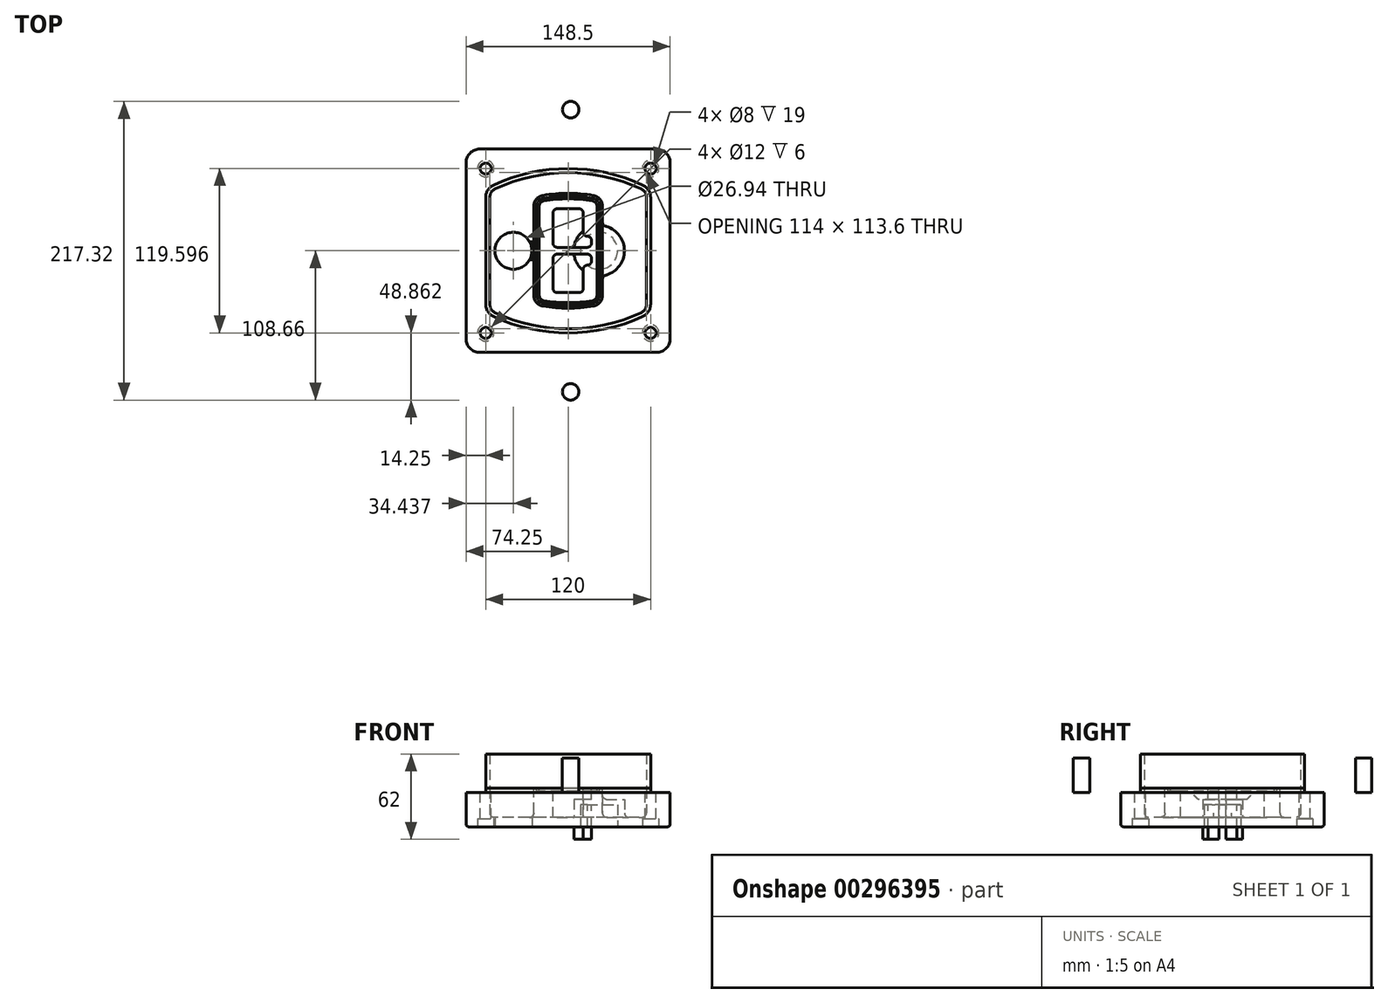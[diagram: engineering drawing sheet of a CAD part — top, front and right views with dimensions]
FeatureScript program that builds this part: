
annotation { "Feature Type Name" : "Feature", "Feature Type Description" : "" }
export const myFeature = defineFeature(function(context is Context, id is Id, definition is map)
    precondition{}
    {
        {
            var Q0;
            Q0=qCreatedBy(makeId("Top.planeOp"),FACE);
            var sketch = newSketch(context, id + "F0", { "sketchPlane" : qUnion([Q0])});
            skPoint(sketch, "E0.rect.middle", {"position": v(0, 0) * mm});
            skLineSegment(sketch, "E1.bottom", {"start": v(-64.25, -74) * mm, "end": v(64.25, -74) * mm});
            skLineSegment(sketch, "E1.top", {"start": v(-64.25, 74) * mm, "end": v(64.25, 74) * mm});
            skLineSegment(sketch, "E1.left", {"start": v(-74.25, -64) * mm, "end": v(-74.25, 64) * mm});
            skLineSegment(sketch, "E1.right", {"start": v(74.25, -64) * mm, "end": v(74.25, 64) * mm});
            skLineSegment(sketch, "E2", {"start": v(-74.25, 74) * mm, "end": v(74.25, -74) * mm, "construction": true});
            skLineSegment(sketch, "E3", {"start": v(74.25, 74) * mm, "end": v(-74.25, -74) * mm, "construction": true});
            skCircle(sketch, "E4", {"center": v(-60, 59.8) * mm, "radius": 4 * mm});
            skCircle(sketch, "E5", {"center": v(60, 59.8) * mm, "radius": 4 * mm});
            skCircle(sketch, "E6", {"center": v(60, -59.8) * mm, "radius": 4 * mm});
            skCircle(sketch, "E7", {"center": v(-60, -59.8) * mm, "radius": 4 * mm});
            skLineSegment(sketch, "E8", {"start": v(-60, 59.8) * mm, "end": v(60, 59.8) * mm, "construction": true});
            skLineSegment(sketch, "E9", {"start": v(60, 59.8) * mm, "end": v(60, -59.8) * mm, "construction": true});
            skLineSegment(sketch, "E10", {"start": v(60, -59.8) * mm, "end": v(-60, -59.8) * mm, "construction": true});
            skLineSegment(sketch, "E11", {"start": v(-60, -59.8) * mm, "end": v(-60, 59.8) * mm, "construction": true});
            skLineSegment(sketch, "E12", {"start": v(-60, 38.79) * mm, "end": v(-60, -38.79) * mm});
            skLineSegment(sketch, "E13", {"start": v(60, 38.79) * mm, "end": v(60, -38.79) * mm});
            skArc(sketch, "E14", {"start": v(54.2, 47.86) * mm, "mid": v(0, 59.8) * mm, "end": v(-54.2, 47.86) * mm});
            skArc(sketch, "E15", {"start": v(-54.2, -47.86) * mm, "mid": v(0, -59.8) * mm, "end": v(54.2, -47.86) * mm});
            skLineSegment(sketch, "E16", {"start": v(-60, 0) * mm, "end": v(60, 0) * mm, "construction": true});
            skPoint(sketch, "E17.visualSharp", {"position": v(-60, -45) * mm});
            skArc(sketch, "E17.filletArc", {"start": v(-60, -38.79) * mm, "mid": v(-58.43, -44.17) * mm, "end": v(-54.2, -47.86) * mm});
            skPoint(sketch, "E18.visualSharp", {"position": v(-60, 45) * mm});
            skArc(sketch, "E18.filletArc", {"start": v(-54.2, 47.86) * mm, "mid": v(-58.43, 44.17) * mm, "end": v(-60, 38.79) * mm});
            skPoint(sketch, "E19.visualSharp", {"position": v(60, 45) * mm});
            skArc(sketch, "E19.filletArc", {"start": v(60, 38.79) * mm, "mid": v(58.43, 44.17) * mm, "end": v(54.2, 47.86) * mm});
            skPoint(sketch, "E20.visualSharp", {"position": v(60, -45) * mm});
            skArc(sketch, "E20.filletArc", {"start": v(54.2, -47.86) * mm, "mid": v(58.43, -44.17) * mm, "end": v(60, -38.79) * mm});
            skPoint(sketch, "E21.visualSharp", {"position": v(-74.25, 74) * mm});
            skArc(sketch, "E21.filletArc", {"start": v(-64.25, 74) * mm, "mid": v(-71.32, 71.07) * mm, "end": v(-74.25, 64) * mm});
            skPoint(sketch, "E22.visualSharp", {"position": v(74.25, 74) * mm});
            skArc(sketch, "E22.filletArc", {"start": v(74.25, 64) * mm, "mid": v(71.32, 71.07) * mm, "end": v(64.25, 74) * mm});
            skPoint(sketch, "E23.visualSharp", {"position": v(74.25, -74) * mm});
            skArc(sketch, "E23.filletArc", {"start": v(64.25, -74) * mm, "mid": v(71.32, -71.07) * mm, "end": v(74.25, -64) * mm});
            skPoint(sketch, "E24.visualSharp", {"position": v(-74.25, -74) * mm});
            skArc(sketch, "E24.filletArc", {"start": v(-74.25, -64) * mm, "mid": v(-71.32, -71.07) * mm, "end": v(-64.25, -74) * mm});
            skArc(sketch, "E25.0", {"start": v(57, 38.79) * mm, "mid": v(55.9, 42.56) * mm, "end": v(52.94, 45.14) * mm});
            skLineSegment(sketch, "E25.1", {"start": v(57, 38.79) * mm, "end": v(57, -38.79) * mm});
            skArc(sketch, "E25.2", {"start": v(52.94, -45.14) * mm, "mid": v(55.9, -42.56) * mm, "end": v(57, -38.79) * mm});
            skArc(sketch, "E25.3", {"start": v(-52.94, -45.14) * mm, "mid": v(0, -56.8) * mm, "end": v(52.94, -45.14) * mm});
            skArc(sketch, "E25.4", {"start": v(-57, -38.79) * mm, "mid": v(-55.9, -42.56) * mm, "end": v(-52.94, -45.14) * mm});
            skArc(sketch, "E25.5", {"start": v(52.94, 45.14) * mm, "mid": v(0, 56.8) * mm, "end": v(-52.94, 45.14) * mm});
            skLineSegment(sketch, "E25.6", {"start": v(-57, 38.79) * mm, "end": v(-57, -38.79) * mm});
            skArc(sketch, "E25.7", {"start": v(-52.94, 45.14) * mm, "mid": v(-55.9, 42.56) * mm, "end": v(-57, 38.79) * mm});
            skArc(sketch, "E26.0", {"start": v(-55.88, 51.5) * mm, "mid": v(-61.8, 46.33) * mm, "end": v(-64, 38.79) * mm});
            skArc(sketch, "E26.1", {"start": v(55.88, 51.5) * mm, "mid": v(0, 63.8) * mm, "end": v(-55.88, 51.5) * mm});
            skArc(sketch, "E26.2", {"start": v(64, 38.79) * mm, "mid": v(61.8, 46.33) * mm, "end": v(55.88, 51.5) * mm});
            skLineSegment(sketch, "E26.3", {"start": v(64, 38.79) * mm, "end": v(64, -38.79) * mm});
            skArc(sketch, "E26.4", {"start": v(55.88, -51.5) * mm, "mid": v(61.8, -46.33) * mm, "end": v(64, -38.79) * mm});
            skLineSegment(sketch, "E26.5", {"start": v(-64, 38.79) * mm, "end": v(-64, -38.79) * mm});
            skArc(sketch, "E26.6", {"start": v(-55.88, -51.5) * mm, "mid": v(0, -63.8) * mm, "end": v(55.88, -51.5) * mm});
            skArc(sketch, "E26.7", {"start": v(-64, -38.79) * mm, "mid": v(-61.8, -46.33) * mm, "end": v(-55.88, -51.5) * mm});
            skSolve(sketch);
        }
        {
            var Q0;
            Q0=makeQuery(id+"F0.imprint","IMPRINT",FACE,{"disambiguationData":[TD([[makeQuery(id+"F0.imprint","IMPRINT",EDGE,{"derivedFrom":sQuery(id+"F0.wireOp",EDGE,"E1.bottom")}),1.0]])]});
            var Q1;
            Q1=makeQuery(id+"F0.imprint","IMPRINT",FACE,{"disambiguationData":[TD([[makeQuery(id+"F0.imprint","IMPRINT",EDGE,{"derivedFrom":sQuery(id+"F0.wireOp",EDGE,"E12")}),1.0]])]});
            var Q2;
            Q2=makeQuery(id+"F0.imprint","IMPRINT",FACE,{"disambiguationData":[TD([[makeQuery(id+"F0.imprint","IMPRINT",EDGE,{"derivedFrom":sQuery(id+"F0.wireOp",EDGE,"E25.0")}),1.0]])]});
            var Q3;
            Q3=makeQuery(id+"F0.imprint","IMPRINT",FACE,{"disambiguationData":[TD([[makeQuery(id+"F0.imprint","IMPRINT",EDGE,{"derivedFrom":sQuery(id+"F0.wireOp",EDGE,"E12")}),-1.0]])]});
            extrude(context, id + "F1", {"entities" : qUnion([Q0, Q1, Q2, Q3]), "oppositeDirection" : true, "depth" : 25 * mm});
        }
        {
            var Q0;
            Q0=makeQuery(id+"F0.imprint","IMPRINT",FACE,{"disambiguationData":[TD([[makeQuery(id+"F0.imprint","IMPRINT",EDGE,{"derivedFrom":sQuery(id+"F0.wireOp",EDGE,"E12")}),1.0]])]});
            extrude(context, id + "F2", {"entities" : qUnion([Q0]), "operationType" : NewBodyOperationType.ADD, "depth" : 3 * mm});
        }
        {
            var Q0;
            Q0=makeQuery(id+"F0.imprint","IMPRINT",FACE,{"disambiguationData":[TD([[makeQuery(id+"F0.imprint","IMPRINT",EDGE,{"derivedFrom":sQuery(id+"F0.wireOp",EDGE,"E25.0")}),1.0]])]});
            extrude(context, id + "F3", {"entities" : qUnion([Q0]), "operationType" : NewBodyOperationType.REMOVE, "oppositeDirection" : true, "depth" : 18 * mm});
        }
        {
            var Q0;
            Q0=makeQuery(id+"F2.opExtrude","CAP_FACE",FACE,{"disambiguationData":[OSD([sQuery(id+"F0.wireOp",EDGE,"E12"),sQuery(id+"F0.wireOp",EDGE,"E13"),sQuery(id+"F0.wireOp",EDGE,"E14"),sQuery(id+"F0.wireOp",EDGE,"E15"),sQuery(id+"F0.wireOp",EDGE,"E17.filletArc"),sQuery(id+"F0.wireOp",EDGE,"E18.filletArc"),sQuery(id+"F0.wireOp",EDGE,"E19.filletArc"),sQuery(id+"F0.wireOp",EDGE,"E20.filletArc"),sQuery(id+"F0.wireOp",EDGE,"E25.0"),sQuery(id+"F0.wireOp",EDGE,"E25.1"),sQuery(id+"F0.wireOp",EDGE,"E25.2"),sQuery(id+"F0.wireOp",EDGE,"E25.3"),sQuery(id+"F0.wireOp",EDGE,"E25.4"),sQuery(id+"F0.wireOp",EDGE,"E25.5"),sQuery(id+"F0.wireOp",EDGE,"E25.6"),sQuery(id+"F0.wireOp",EDGE,"E25.7")])],"isStart":false});
            var sketch = newSketch(context, id + "F4", { "sketchPlane" : qUnion([Q0])});
            skArc(sketch, "E27.0", {"start": v(-18.32, -40.28) * mm, "mid": v(0, -41.8) * mm, "end": v(18.32, -40.28) * mm});
            skArc(sketch, "E28.0", {"start": v(18.32, 40.28) * mm, "mid": v(0, 41.8) * mm, "end": v(-18.32, 40.28) * mm});
            skLineSegment(sketch, "E29", {"start": v(-25, 32.39) * mm, "end": v(-25, -32.39) * mm});
            skLineSegment(sketch, "E30", {"start": v(25, 32.39) * mm, "end": v(25, -32.39) * mm});
            skLineSegment(sketch, "E31", {"start": v(-25, 38.95) * mm, "end": v(25, 38.95) * mm, "construction": true});
            skLineSegment(sketch, "E32", {"start": v(-25, -38.95) * mm, "end": v(25, -38.95) * mm, "construction": true});
            skPoint(sketch, "E33.visualSharp", {"position": v(-25, 38.95) * mm});
            skArc(sketch, "E33.filletArc", {"start": v(-18.32, 40.28) * mm, "mid": v(-23.1, 37.56) * mm, "end": v(-25, 32.39) * mm});
            skPoint(sketch, "E34.visualSharp", {"position": v(25, 38.95) * mm});
            skArc(sketch, "E34.filletArc", {"start": v(25, 32.39) * mm, "mid": v(23.1, 37.56) * mm, "end": v(18.32, 40.28) * mm});
            skPoint(sketch, "E35.visualSharp", {"position": v(25, -38.95) * mm});
            skArc(sketch, "E35.filletArc", {"start": v(18.32, -40.28) * mm, "mid": v(23.1, -37.56) * mm, "end": v(25, -32.39) * mm});
            skPoint(sketch, "E36.visualSharp", {"position": v(-25, -38.95) * mm});
            skArc(sketch, "E36.filletArc", {"start": v(-25, -32.39) * mm, "mid": v(-23.1, -37.56) * mm, "end": v(-18.32, -40.28) * mm});
            skArc(sketch, "E37.0", {"start": v(52.94, 45.14) * mm, "mid": v(0, 56.8) * mm, "end": v(-52.94, 45.14) * mm});
            skArc(sketch, "E37.1", {"start": v(-52.94, 45.14) * mm, "mid": v(-55.9, 42.56) * mm, "end": v(-57, 38.79) * mm});
            skLineSegment(sketch, "E37.2", {"start": v(-57, 38.79) * mm, "end": v(-57, -38.79) * mm});
            skArc(sketch, "E37.3", {"start": v(-57, -38.79) * mm, "mid": v(-55.9, -42.56) * mm, "end": v(-52.94, -45.14) * mm});
            skArc(sketch, "E37.4", {"start": v(-52.94, -45.14) * mm, "mid": v(0, -56.8) * mm, "end": v(52.94, -45.14) * mm});
            skArc(sketch, "E37.5", {"start": v(52.94, -45.14) * mm, "mid": v(55.9, -42.56) * mm, "end": v(57, -38.79) * mm});
            skLineSegment(sketch, "E37.6", {"start": v(57, 38.79) * mm, "end": v(57, -38.79) * mm});
            skArc(sketch, "E37.7", {"start": v(57, 38.79) * mm, "mid": v(55.9, 42.56) * mm, "end": v(52.94, 45.14) * mm});
            skLineSegment(sketch, "E38.0", {"start": v(23, 32.39) * mm, "end": v(23, -32.39) * mm});
            skArc(sketch, "E38.1", {"start": v(17.99, -38.3) * mm, "mid": v(21.58, -36.26) * mm, "end": v(23, -32.39) * mm});
            skArc(sketch, "E38.2", {"start": v(-17.99, -38.3) * mm, "mid": v(0, -39.8) * mm, "end": v(17.99, -38.3) * mm});
            skArc(sketch, "E38.3", {"start": v(-23, -32.39) * mm, "mid": v(-21.58, -36.26) * mm, "end": v(-17.99, -38.3) * mm});
            skLineSegment(sketch, "E38.4", {"start": v(-23, 32.39) * mm, "end": v(-23, -32.39) * mm});
            skArc(sketch, "E38.5", {"start": v(23, 32.39) * mm, "mid": v(21.58, 36.26) * mm, "end": v(17.99, 38.3) * mm});
            skArc(sketch, "E38.6", {"start": v(-17.99, 38.3) * mm, "mid": v(-21.58, 36.26) * mm, "end": v(-23, 32.39) * mm});
            skArc(sketch, "E38.7", {"start": v(17.99, 38.3) * mm, "mid": v(0, 39.8) * mm, "end": v(-17.99, 38.3) * mm});
            skArc(sketch, "E39.0", {"start": v(21, 32.39) * mm, "mid": v(20.05, 34.97) * mm, "end": v(17.66, 36.33) * mm});
            skLineSegment(sketch, "E39.1", {"start": v(21, 32.39) * mm, "end": v(21, -32.39) * mm});
            skArc(sketch, "E39.2", {"start": v(17.66, -36.33) * mm, "mid": v(20.05, -34.97) * mm, "end": v(21, -32.39) * mm});
            skArc(sketch, "E39.3", {"start": v(-17.66, -36.33) * mm, "mid": v(0, -37.8) * mm, "end": v(17.66, -36.33) * mm});
            skArc(sketch, "E39.4", {"start": v(-21, -32.39) * mm, "mid": v(-20.05, -34.97) * mm, "end": v(-17.66, -36.33) * mm});
            skArc(sketch, "E39.5", {"start": v(17.66, 36.33) * mm, "mid": v(0, 37.8) * mm, "end": v(-17.66, 36.33) * mm});
            skLineSegment(sketch, "E39.6", {"start": v(-21, 32.39) * mm, "end": v(-21, -32.39) * mm});
            skArc(sketch, "E39.7", {"start": v(-17.66, 36.33) * mm, "mid": v(-20.05, 34.97) * mm, "end": v(-21, 32.39) * mm});
            skLineSegment(sketch, "E40", {"start": v(-25, 0) * mm, "end": v(25, 0) * mm, "construction": true});
            skLineSegment(sketch, "E41", {"start": v(-11, 5.5) * mm, "end": v(-11, 27.5) * mm});
            skLineSegment(sketch, "E42", {"start": v(-8, 30.5) * mm, "end": v(8, 30.5) * mm});
            skLineSegment(sketch, "E43", {"start": v(11, 27.5) * mm, "end": v(11, 13.5) * mm});
            skLineSegment(sketch, "E44", {"start": v(14, 10.5) * mm, "end": v(14, 10.5) * mm});
            skLineSegment(sketch, "E45", {"start": v(17, 7.5) * mm, "end": v(17, 5.5) * mm});
            skLineSegment(sketch, "E46", {"start": v(14, 2.5) * mm, "end": v(-8, 2.5) * mm});
            skPoint(sketch, "E47.visualSharp", {"position": v(-11, 30.5) * mm});
            skArc(sketch, "E47.filletArc", {"start": v(-8, 30.5) * mm, "mid": v(-10.12, 29.62) * mm, "end": v(-11, 27.5) * mm});
            skPoint(sketch, "E48.visualSharp", {"position": v(11, 30.5) * mm});
            skArc(sketch, "E48.filletArc", {"start": v(11, 27.5) * mm, "mid": v(10.12, 29.62) * mm, "end": v(8, 30.5) * mm});
            skPoint(sketch, "E49.visualSharp", {"position": v(11, 10.5) * mm});
            skArc(sketch, "E49.filletArc", {"start": v(11, 13.5) * mm, "mid": v(11.88, 11.38) * mm, "end": v(14, 10.5) * mm});
            skPoint(sketch, "E50.visualSharp", {"position": v(17, 10.5) * mm});
            skArc(sketch, "E50.filletArc", {"start": v(17, 7.5) * mm, "mid": v(16.12, 9.62) * mm, "end": v(14, 10.5) * mm});
            skPoint(sketch, "E51.visualSharp", {"position": v(17, 2.5) * mm});
            skArc(sketch, "E51.filletArc", {"start": v(14, 2.5) * mm, "mid": v(16.12, 3.38) * mm, "end": v(17, 5.5) * mm});
            skPoint(sketch, "E52.visualSharp", {"position": v(-11, 2.5) * mm});
            skArc(sketch, "E52.filletArc", {"start": v(-11, 5.5) * mm, "mid": v(-10.12, 3.38) * mm, "end": v(-8, 2.5) * mm});
            skLineSegment(sketch, "E53.0.MirrorCS", {"start": v(14, -2.5) * mm, "end": v(-8, -2.5) * mm});
            skArc(sketch, "E54.0.MirrorCS", {"start": v(-11, -5.5) * mm, "mid": v(-10.12, -3.38) * mm, "end": v(-8, -2.5) * mm});
            skLineSegment(sketch, "E55.0.MirrorCS", {"start": v(-11, -5.5) * mm, "end": v(-11, -27.5) * mm});
            skArc(sketch, "E56.0.MirrorCS", {"start": v(-8, -30.5) * mm, "mid": v(-10.12, -29.62) * mm, "end": v(-11, -27.5) * mm});
            skLineSegment(sketch, "E57.0.MirrorCS", {"start": v(-8, -30.5) * mm, "end": v(8, -30.5) * mm});
            skArc(sketch, "E58.0.MirrorCS", {"start": v(11, -27.5) * mm, "mid": v(10.12, -29.62) * mm, "end": v(8, -30.5) * mm});
            skLineSegment(sketch, "E59.0.MirrorCS", {"start": v(11, -27.5) * mm, "end": v(11, -13.5) * mm});
            skArc(sketch, "E60.0.MirrorCS", {"start": v(11, -13.5) * mm, "mid": v(11.88, -11.38) * mm, "end": v(14, -10.5) * mm});
            skArc(sketch, "E61.0.MirrorCS", {"start": v(17, -7.5) * mm, "mid": v(16.12, -9.62) * mm, "end": v(14, -10.5) * mm});
            skLineSegment(sketch, "E62.0.MirrorCS", {"start": v(17, -7.5) * mm, "end": v(17, -5.5) * mm});
            skArc(sketch, "E63.0.MirrorCS", {"start": v(14, -2.5) * mm, "mid": v(16.12, -3.38) * mm, "end": v(17, -5.5) * mm});
            skSolve(sketch);
        }
        {
            var Q0;
            Q0=makeQuery(id+"F4.imprint","IMPRINT",FACE,{"disambiguationData":[TD([[makeQuery(id+"F4.imprint","IMPRINT",EDGE,{"derivedFrom":sQuery(id+"F4.wireOp",EDGE,"E27.0")}),1.0]])]});
            var Q1;
            Q1=makeQuery(id+"F4.imprint","IMPRINT",FACE,{"disambiguationData":[TD([[makeQuery(id+"F4.imprint","IMPRINT",EDGE,{"derivedFrom":sQuery(id+"F4.wireOp",EDGE,"E38.0")}),-1.0]])]});
            var Q2;
            Q2=makeQuery(id+"F4.imprint","IMPRINT",FACE,{"disambiguationData":[TD([[makeQuery(id+"F4.imprint","IMPRINT",EDGE,{"derivedFrom":sQuery(id+"F4.wireOp",EDGE,"E39.0")}),1.0]])]});
            extrude(context, id + "F5", {"entities" : qUnion([Q0, Q1, Q2]), "operationType" : NewBodyOperationType.ADD, "endBound" : BoundingType.UP_TO_NEXT, "oppositeDirection" : true, "depth" : 25 * mm});
        }
        {
            var Q0;
            Q0=makeQuery(id+"F4.imprint","IMPRINT",FACE,{"disambiguationData":[TD([[makeQuery(id+"F4.imprint","IMPRINT",EDGE,{"derivedFrom":sQuery(id+"F4.wireOp",EDGE,"E38.0")}),-1.0]])]});
            extrude(context, id + "F6", {"entities" : qUnion([Q0]), "operationType" : NewBodyOperationType.REMOVE, "oppositeDirection" : true, "depth" : 2 * mm});
        }
        {
            var Q0;
            Q0=makeQuery(id+"F1.opExtrude","CAP_FACE",FACE,{"disambiguationData":[OSD([sQuery(id+"F0.wireOp",EDGE,"E1.bottom"),sQuery(id+"F0.wireOp",EDGE,"E1.top"),sQuery(id+"F0.wireOp",EDGE,"E1.left"),sQuery(id+"F0.wireOp",EDGE,"E1.right"),sQuery(id+"F0.wireOp",EDGE,"E4"),sQuery(id+"F0.wireOp",EDGE,"E5"),sQuery(id+"F0.wireOp",EDGE,"E6"),sQuery(id+"F0.wireOp",EDGE,"E7"),sQuery(id+"F0.wireOp",EDGE,"E21.filletArc"),sQuery(id+"F0.wireOp",EDGE,"E22.filletArc"),sQuery(id+"F0.wireOp",EDGE,"E23.filletArc"),sQuery(id+"F0.wireOp",EDGE,"E24.filletArc")])],"isStart":false});
            var sketch = newSketch(context, id + "F7", { "sketchPlane" : qUnion([Q0])});
            skCircle(sketch, "E64", {"center": v(22.5, 0) * mm, "radius": 13.47 * mm});
            skCircle(sketch, "E65", {"center": v(-39.81, 0) * mm, "radius": 13.47 * mm});
            skLineSegment(sketch, "E66", {"start": v(74.25, 0) * mm, "end": v(-74.25, 0) * mm});
            skCircle(sketch, "E67", {"center": v(22.5, 0) * mm, "radius": 18.47 * mm});
            skCircle(sketch, "E68", {"center": v(60, -59.8) * mm, "radius": 6 * mm});
            skCircle(sketch, "E69", {"center": v(-60, -59.8) * mm, "radius": 6 * mm});
            skCircle(sketch, "E70", {"center": v(-60, 59.8) * mm, "radius": 6 * mm});
            skCircle(sketch, "E71", {"center": v(60, 59.8) * mm, "radius": 6 * mm});
            skSolve(sketch);
        }
        {
            var Q0;
            {var subQ1=sQuery(id+"F7.wireOp",EDGE,"E66");var subQ4=sQuery(id+"F7.wireOp",EDGE,"E64");var subQ6=makeQuery(id+"F7.imprint","INTERSECT",VERTEX,{"disambiguationData":[OD(0.0)],"derivedFrom":[subQ4,subQ1]});Q0=makeQuery(id+"F7.imprint","IMPRINT",FACE,{"disambiguationData":[TD([[makeQuery(id+"F7.imprint","IMPRINT",EDGE,{"disambiguationData":[TD([[subQ6,-1.0]])],"derivedFrom":subQ4}),-1.0]])]});}
            var Q1;
            {var subQ0=sQuery(id+"F7.wireOp",EDGE,"E66");var subQ1=sQuery(id+"F7.wireOp",EDGE,"E64");var subQ3=makeQuery(id+"F7.imprint","INTERSECT",VERTEX,{"disambiguationData":[OD(0.0)],"derivedFrom":[subQ1,subQ0]});Q1=makeQuery(id+"F7.imprint","IMPRINT",FACE,{"disambiguationData":[TD([[makeQuery(id+"F7.imprint","IMPRINT",EDGE,{"disambiguationData":[TD([[subQ3,-1.0]])],"derivedFrom":subQ1}),1.0]])]});}
            var Q2;
            {var subQ0=sQuery(id+"F7.wireOp",EDGE,"E66");var subQ1=sQuery(id+"F7.wireOp",EDGE,"E64");var subQ3=makeQuery(id+"F7.imprint","INTERSECT",VERTEX,{"disambiguationData":[OD(0.0)],"derivedFrom":[subQ1,subQ0]});Q2=makeQuery(id+"F7.imprint","IMPRINT",FACE,{"disambiguationData":[TD([[makeQuery(id+"F7.imprint","IMPRINT",EDGE,{"disambiguationData":[TD([[subQ3,1.0]])],"derivedFrom":subQ1}),1.0]])]});}
            var Q3;
            {var subQ1=sQuery(id+"F7.wireOp",EDGE,"E66");var subQ4=sQuery(id+"F7.wireOp",EDGE,"E64");var subQ6=makeQuery(id+"F7.imprint","INTERSECT",VERTEX,{"disambiguationData":[OD(0.0)],"derivedFrom":[subQ4,subQ1]});Q3=makeQuery(id+"F7.imprint","IMPRINT",FACE,{"disambiguationData":[TD([[makeQuery(id+"F7.imprint","IMPRINT",EDGE,{"disambiguationData":[TD([[subQ6,1.0]])],"derivedFrom":subQ4}),-1.0]])]});}
            extrude(context, id + "F8", {"entities" : qUnion([Q0, Q1, Q2, Q3]), "operationType" : NewBodyOperationType.ADD, "oppositeDirection" : true, "depth" : 20 * mm});
        }
        {
            var Q0;
            {var subQ0=sQuery(id+"F7.wireOp",EDGE,"E66");var subQ1=sQuery(id+"F7.wireOp",EDGE,"E64");var subQ3=makeQuery(id+"F7.imprint","INTERSECT",VERTEX,{"disambiguationData":[OD(0.0)],"derivedFrom":[subQ1,subQ0]});Q0=makeQuery(id+"F7.imprint","IMPRINT",FACE,{"disambiguationData":[TD([[makeQuery(id+"F7.imprint","IMPRINT",EDGE,{"disambiguationData":[TD([[subQ3,-1.0]])],"derivedFrom":subQ1}),1.0]])]});}
            var Q1;
            {var subQ0=sQuery(id+"F7.wireOp",EDGE,"E66");var subQ1=sQuery(id+"F7.wireOp",EDGE,"E64");var subQ3=makeQuery(id+"F7.imprint","INTERSECT",VERTEX,{"disambiguationData":[OD(0.0)],"derivedFrom":[subQ1,subQ0]});Q1=makeQuery(id+"F7.imprint","IMPRINT",FACE,{"disambiguationData":[TD([[makeQuery(id+"F7.imprint","IMPRINT",EDGE,{"disambiguationData":[TD([[subQ3,1.0]])],"derivedFrom":subQ1}),1.0]])]});}
            extrude(context, id + "F9", {"entities" : qUnion([Q0, Q1]), "operationType" : NewBodyOperationType.REMOVE, "oppositeDirection" : true, "depth" : 16 * mm});
        }
        {
            var Q0;
            {var subQ0=sQuery(id+"F7.wireOp",EDGE,"E66");var subQ1=sQuery(id+"F7.wireOp",EDGE,"E65");var subQ3=makeQuery(id+"F7.imprint","INTERSECT",VERTEX,{"disambiguationData":[OD(0.0)],"derivedFrom":[subQ1,subQ0]});Q0=makeQuery(id+"F7.imprint","IMPRINT",FACE,{"disambiguationData":[TD([[makeQuery(id+"F7.imprint","IMPRINT",EDGE,{"disambiguationData":[TD([[subQ3,-1.0]])],"derivedFrom":subQ1}),1.0]])]});}
            var Q1;
            {var subQ0=sQuery(id+"F7.wireOp",EDGE,"E66");var subQ1=sQuery(id+"F7.wireOp",EDGE,"E65");var subQ3=makeQuery(id+"F7.imprint","INTERSECT",VERTEX,{"disambiguationData":[OD(0.0)],"derivedFrom":[subQ1,subQ0]});Q1=makeQuery(id+"F7.imprint","IMPRINT",FACE,{"disambiguationData":[TD([[makeQuery(id+"F7.imprint","IMPRINT",EDGE,{"disambiguationData":[TD([[subQ3,1.0]])],"derivedFrom":subQ1}),1.0]])]});}
            extrude(context, id + "F10", {"entities" : qUnion([Q0, Q1]), "operationType" : NewBodyOperationType.REMOVE, "oppositeDirection" : true, "depth" : 25 * mm});
        }
        {
            var Q0;
            Q0=makeQuery(id+"F7.imprint","IMPRINT",FACE,{"disambiguationData":[TD([[makeQuery(id+"F7.imprint","IMPRINT",EDGE,{"derivedFrom":sQuery(id+"F7.wireOp",EDGE,"E68")}),1.0]])]});
            var Q1;
            Q1=makeQuery(id+"F7.imprint","IMPRINT",FACE,{"disambiguationData":[TD([[makeQuery(id+"F7.imprint","IMPRINT",EDGE,{"derivedFrom":makeQuery(id+"F1.opExtrude","CAP_EDGE",EDGE,{"disambiguationData":[OSD([sQuery(id+"F0.wireOp",EDGE,"E5")])],"isStart":false})}),-1.0]])]});
            var Q2;
            Q2=makeQuery(id+"F7.imprint","IMPRINT",FACE,{"disambiguationData":[TD([[makeQuery(id+"F7.imprint","IMPRINT",EDGE,{"derivedFrom":sQuery(id+"F7.wireOp",EDGE,"E69")}),1.0]])]});
            var Q3;
            Q3=makeQuery(id+"F7.imprint","IMPRINT",FACE,{"disambiguationData":[TD([[makeQuery(id+"F7.imprint","IMPRINT",EDGE,{"derivedFrom":makeQuery(id+"F1.opExtrude","CAP_EDGE",EDGE,{"disambiguationData":[OSD([sQuery(id+"F0.wireOp",EDGE,"E4")])],"isStart":false})}),-1.0]])]});
            var Q4;
            Q4=makeQuery(id+"F7.imprint","IMPRINT",FACE,{"disambiguationData":[TD([[makeQuery(id+"F7.imprint","IMPRINT",EDGE,{"derivedFrom":sQuery(id+"F7.wireOp",EDGE,"E70")}),1.0]])]});
            var Q5;
            Q5=makeQuery(id+"F7.imprint","IMPRINT",FACE,{"disambiguationData":[TD([[makeQuery(id+"F7.imprint","IMPRINT",EDGE,{"derivedFrom":makeQuery(id+"F1.opExtrude","CAP_EDGE",EDGE,{"disambiguationData":[OSD([sQuery(id+"F0.wireOp",EDGE,"E7")])],"isStart":false})}),-1.0]])]});
            var Q6;
            Q6=makeQuery(id+"F7.imprint","IMPRINT",FACE,{"disambiguationData":[TD([[makeQuery(id+"F7.imprint","IMPRINT",EDGE,{"derivedFrom":sQuery(id+"F7.wireOp",EDGE,"E71")}),1.0]])]});
            var Q7;
            Q7=makeQuery(id+"F7.imprint","IMPRINT",FACE,{"disambiguationData":[TD([[makeQuery(id+"F7.imprint","IMPRINT",EDGE,{"derivedFrom":makeQuery(id+"F1.opExtrude","CAP_EDGE",EDGE,{"disambiguationData":[OSD([sQuery(id+"F0.wireOp",EDGE,"E6")])],"isStart":false})}),-1.0]])]});
            extrude(context, id + "F11", {"entities" : qUnion([Q0, Q1, Q2, Q3, Q4, Q5, Q6, Q7]), "operationType" : NewBodyOperationType.REMOVE, "oppositeDirection" : true, "depth" : 6 * mm});
        }
        {
            var Q0;
            Q0=makeQuery(id+"F9.boolean.opBoolean","COPY",FACE,{"derivedFrom":makeQuery(id+"F9.opExtrude","CAP_FACE",FACE,{"disambiguationData":[OSD([sQuery(id+"F7.wireOp",EDGE,"E64")])],"isStart":false})});
            var sketch = newSketch(context, id + "F12", { "sketchPlane" : qUnion([Q0])});
            skArc(sketch, "E72.0", {"start": v(11, 14.45) * mm, "mid": v(6.45, 9.13) * mm, "end": v(4.2, 2.5) * mm});
            skArc(sketch, "E72.1", {"start": v(4.2, -2.5) * mm, "mid": v(6.45, -9.13) * mm, "end": v(11, -14.45) * mm});
            skLineSegment(sketch, "E73", {"start": v(4.2, -2.5) * mm, "end": v(14, -2.5) * mm});
            skLineSegment(sketch, "E74.0", {"start": v(14, 2.5) * mm, "end": v(4.2, 2.5) * mm});
            skArc(sketch, "E74.1", {"start": v(14, 2.5) * mm, "mid": v(16.12, 3.38) * mm, "end": v(17, 5.5) * mm});
            skLineSegment(sketch, "E74.2", {"start": v(17, 7.5) * mm, "end": v(17, 5.5) * mm});
            skArc(sketch, "E74.3", {"start": v(17, 7.5) * mm, "mid": v(16.12, 9.62) * mm, "end": v(14, 10.5) * mm});
            skArc(sketch, "E74.4", {"start": v(11, 13.5) * mm, "mid": v(11.88, 11.38) * mm, "end": v(14, 10.5) * mm});
            skLineSegment(sketch, "E74.5", {"start": v(11, 14.45) * mm, "end": v(11, 13.5) * mm});
            skLineSegment(sketch, "E74.7", {"start": v(14, -2.5) * mm, "end": v(4.2, -2.5) * mm});
            skArc(sketch, "E74.8", {"start": v(14, -2.5) * mm, "mid": v(16.12, -3.38) * mm, "end": v(17, -5.5) * mm});
            skLineSegment(sketch, "E74.9", {"start": v(17, -7.5) * mm, "end": v(17, -5.5) * mm});
            skArc(sketch, "E74.10", {"start": v(17, -7.5) * mm, "mid": v(16.12, -9.62) * mm, "end": v(14, -10.5) * mm});
            skArc(sketch, "E74.11", {"start": v(11, -13.5) * mm, "mid": v(11.88, -11.38) * mm, "end": v(14, -10.5) * mm});
            skLineSegment(sketch, "E74.12", {"start": v(11, -14.45) * mm, "end": v(11, -13.5) * mm});
            skPoint(sketch, "E75.orphan", {"position": v(11, -27.5) * mm});
            skPoint(sketch, "E76.orphan", {"position": v(-8, -2.5) * mm});
            skPoint(sketch, "E77.orphan", {"position": v(-8, 2.5) * mm});
            skPoint(sketch, "E78.orphan", {"position": v(11, 27.5) * mm});
            skSolve(sketch);
        }
        {
            var Q0;
            {var subQ7=sQuery(id+"F12.wireOp",EDGE,"E72.0");var subQ14=sQuery(id+"F12.wireOp",EDGE,"E72.1");var subQ16=sQuery(id+"F12.wireOp",EDGE,"E74.1");var subQ18=sQuery(id+"F12.wireOp",EDGE,"E74.8");Q0=qUnion([makeQuery(id+"F12.imprint","IMPRINT",FACE,{"disambiguationData":[TD([[makeQuery(id+"F12.imprint","IMPRINT",EDGE,{"derivedFrom":subQ7}),1.0]])]}),makeQuery(id+"F12.imprint","IMPRINT",FACE,{"disambiguationData":[TD([[makeQuery(id+"F12.imprint","IMPRINT",EDGE,{"derivedFrom":subQ14}),1.0]])]}),makeQuery(id+"F12.imprint","IMPRINT",FACE,{"disambiguationData":[TD([[makeQuery(id+"F12.imprint","IMPRINT",EDGE,{"derivedFrom":subQ16}),1.0]])]}),makeQuery(id+"F12.imprint","IMPRINT",FACE,{"disambiguationData":[TD([[makeQuery(id+"F12.imprint","IMPRINT",EDGE,{"derivedFrom":subQ18}),-1.0]])]})]);}
            var Q1;
            Q1=makeQuery(id+"F5.boolean.opBoolean","SPLIT",FACE,{"disambiguationData":[TD([makeQuery(id+"F5.opExtrude","SWEPT_FACE",FACE,{"disambiguationData":[OSD([sQuery(id+"F4.wireOp",EDGE,"E41")])]})])],"derivedFrom":makeQuery(id+"F3.boolean.opBoolean","COPY",FACE,{"derivedFrom":makeQuery(id+"F3.opExtrude","CAP_FACE",FACE,{"disambiguationData":[OSD([sQuery(id+"F0.wireOp",EDGE,"E25.0"),sQuery(id+"F0.wireOp",EDGE,"E25.1"),sQuery(id+"F0.wireOp",EDGE,"E25.2"),sQuery(id+"F0.wireOp",EDGE,"E25.3"),sQuery(id+"F0.wireOp",EDGE,"E25.4"),sQuery(id+"F0.wireOp",EDGE,"E25.5"),sQuery(id+"F0.wireOp",EDGE,"E25.6"),sQuery(id+"F0.wireOp",EDGE,"E25.7")])],"isStart":false})})});
            extrude(context, id + "F13", {"entities" : qUnion([Q0]), "operationType" : NewBodyOperationType.REMOVE, "endBound" : BoundingType.UP_TO_SURFACE, "endBoundEntityFace" : qUnion([Q1]), "depth" : 25 * mm});
        }
        {
            var Q0;
            Q0=makeQuery(id+"F3.boolean.opBoolean","COPY",EDGE,{"derivedFrom":makeQuery(id+"F3.opExtrude","CAP_EDGE",EDGE,{"disambiguationData":[OSD([sQuery(id+"F0.wireOp",EDGE,"E25.6")])],"isStart":false})});
            var Q1;
            Q1=makeQuery(id+"F8.boolean.opBoolean","INTERSECT",EDGE,{"derivedFrom":[makeQuery(id+"F5.opExtrude","SWEPT_FACE",FACE,{"disambiguationData":[OSD([sQuery(id+"F4.wireOp",EDGE,"E30")])]}),makeQuery(id+"F8.opExtrude","CAP_FACE",FACE,{"disambiguationData":[OSD([sQuery(id+"F7.wireOp",EDGE,"E67")])],"isStart":false})]});
            var Q2;
            Q2=makeQuery(id+"F8.boolean.opBoolean","INTERSECT",EDGE,{"disambiguationData":[OD(1.0)],"derivedFrom":[makeQuery(id+"F5.opExtrude","SWEPT_FACE",FACE,{"disambiguationData":[OSD([sQuery(id+"F4.wireOp",EDGE,"E30")])]}),makeQuery(id+"F8.opExtrude","SWEPT_FACE",FACE,{"disambiguationData":[OSD([sQuery(id+"F7.wireOp",EDGE,"E67")])]})]});
            var Q3;
            {var subQ0=sQuery(id+"F4.wireOp",EDGE,"E30");Q3=makeQuery(id+"F8.boolean.opBoolean","SPLIT",EDGE,{"disambiguationData":[TD([makeQuery(id+"F5.opExtrude","SWEPT_FACE",FACE,{"disambiguationData":[OSD([sQuery(id+"F4.wireOp",EDGE,"E35.filletArc")])]})])],"derivedFrom":makeQuery(id+"F5.opExtrude","CAP_EDGE",EDGE,{"disambiguationData":[OSD([subQ0])],"isStart":false})});}
            var Q4;
            {var subQ0=sQuery(id+"F0.wireOp",EDGE,"E25.7");var subQ1=sQuery(id+"F0.wireOp",EDGE,"E25.1");var subQ2=sQuery(id+"F0.wireOp",EDGE,"E25.6");var subQ3=sQuery(id+"F0.wireOp",EDGE,"E25.5");var subQ4=sQuery(id+"F0.wireOp",EDGE,"E25.4");var subQ5=sQuery(id+"F0.wireOp",EDGE,"E25.0");var subQ6=sQuery(id+"F0.wireOp",EDGE,"E25.2");var subQ7=sQuery(id+"F0.wireOp",EDGE,"E25.3");Q4=makeQuery(id+"F8.boolean.opBoolean","INTERSECT",EDGE,{"derivedFrom":[makeQuery(id+"F5.boolean.opBoolean","SPLIT",FACE,{"disambiguationData":[TD([makeQuery(id+"F2.opExtrude","SWEPT_FACE",FACE,{"disambiguationData":[OSD([subQ5])]})])],"derivedFrom":makeQuery(id+"F3.boolean.opBoolean","COPY",FACE,{"derivedFrom":makeQuery(id+"F3.opExtrude","CAP_FACE",FACE,{"disambiguationData":[OSD([subQ5,subQ1,subQ6,subQ7,subQ4,subQ3,subQ2,subQ0])],"isStart":false})})}),makeQuery(id+"F8.opExtrude","SWEPT_FACE",FACE,{"disambiguationData":[OSD([sQuery(id+"F7.wireOp",EDGE,"E67")])]})]});}
            var Q5;
            Q5=makeQuery(id+"F8.boolean.opBoolean","INTERSECT",EDGE,{"disambiguationData":[OD(0.0)],"derivedFrom":[makeQuery(id+"F5.opExtrude","SWEPT_FACE",FACE,{"disambiguationData":[OSD([sQuery(id+"F4.wireOp",EDGE,"E30")])]}),makeQuery(id+"F8.opExtrude","SWEPT_FACE",FACE,{"disambiguationData":[OSD([sQuery(id+"F7.wireOp",EDGE,"E67")])]})]});
            fillet(context, id + "F14", {"entities" : qUnion([Q0, Q1, Q2, Q3, Q4, Q5]), "radius" : 3 * mm, "tangentPropagation" : true, "allowEdgeOverflow" : false});
        }
        {
            var Q0;
            Q0=makeQuery(id+"F1.opExtrude","CAP_EDGE",EDGE,{"disambiguationData":[OSD([sQuery(id+"F0.wireOp",EDGE,"E1.bottom")])],"isStart":false});
            fillet(context, id + "F15", {"entities" : qUnion([Q0]), "radius" : 2 * mm, "tangentPropagation" : true, "allowEdgeOverflow" : false});
        }
        {
            var Q0;
            Q0 = qSketchRegion(id + "F12", true);
            extrude(context, id + "F16", {"entities" : qUnion([Q0]), "operationType" : NewBodyOperationType.ADD, "depth" : 25 * mm});
        }
        {
            var Q0;
            Q0=qCreatedBy(makeId("Top.planeOp"),FACE);
            var sketch = newSketch(context, id + "F17", { "sketchPlane" : qUnion([Q0])});
            skLineSegment(sketch, "E79", {"start": v(26.76, 75.63) * mm, "end": v(16.86, 90.66) * mm});
            skLineSegment(sketch, "E80", {"start": v(16.86, 90.66) * mm, "end": v(16.86, 102.66) * mm});
            skArc(sketch, "E81", {"start": v(16.86, 102.66) * mm, "mid": v(1.86, 117.66) * mm, "end": v(-13.14, 102.66) * mm});
            skLineSegment(sketch, "E82", {"start": v(-13.14, 102.66) * mm, "end": v(-13.14, 90.66) * mm});
            skLineSegment(sketch, "E83", {"start": v(-13.14, 90.66) * mm, "end": v(-21.62, 74.78) * mm});
            skCircle(sketch, "E84", {"center": v(1.86, 102.66) * mm, "radius": 6 * mm});
            skLineSegment(sketch, "E85", {"start": v(1.86, 102.66) * mm, "end": v(1.86, 72.66) * mm, "construction": true});
            skLineSegment(sketch, "E86", {"start": v(-74.8, 0) * mm, "end": v(74.55, 0) * mm, "construction": true});
            skLineSegment(sketch, "E87.MirrorCS", {"start": v(-13.14, -238.66) * mm, "end": v(-21.62, -222.78) * mm});
            skLineSegment(sketch, "E88.MirrorCS", {"start": v(-13.14, -250.66) * mm, "end": v(-13.14, -238.66) * mm});
            skArc(sketch, "E89.MirrorCS", {"start": v(16.86, -250.66) * mm, "mid": v(1.86, -265.66) * mm, "end": v(-13.14, -250.66) * mm});
            skLineSegment(sketch, "E90.MirrorCS", {"start": v(16.86, -238.66) * mm, "end": v(16.86, -250.66) * mm});
            skLineSegment(sketch, "E91.MirrorCS", {"start": v(26.76, -223.63) * mm, "end": v(16.86, -238.66) * mm});
            skLineSegment(sketch, "E92.MirrorCS", {"start": v(1.86, -250.66) * mm, "end": v(1.86, -220.66) * mm, "construction": true});
            skLineSegment(sketch, "E93.MirrorCS", {"start": v(-13.14, -90.66) * mm, "end": v(-21.62, -74.78) * mm});
            skLineSegment(sketch, "E94.MirrorCS", {"start": v(1.86, -102.66) * mm, "end": v(1.86, -72.66) * mm, "construction": true});
            skCircle(sketch, "E95.MirrorC", {"center": v(1.86, -102.66) * mm, "radius": 6 * mm});
            skArc(sketch, "E96.MirrorCS", {"start": v(16.86, -102.66) * mm, "mid": v(1.86, -117.66) * mm, "end": v(-13.14, -102.66) * mm});
            skLineSegment(sketch, "E97.MirrorCS", {"start": v(16.86, -90.66) * mm, "end": v(16.86, -102.66) * mm});
            skLineSegment(sketch, "E98.MirrorCS", {"start": v(-13.14, -102.66) * mm, "end": v(-13.14, -90.66) * mm});
            skLineSegment(sketch, "E99.MirrorCS", {"start": v(26.76, -75.63) * mm, "end": v(16.86, -90.66) * mm});
            skSolve(sketch);
        }
        {
            var Q0;
            Q0=makeQuery(id+"F2.opExtrude","CAP_FACE",FACE,{"disambiguationData":[OSD([sQuery(id+"F0.wireOp",EDGE,"E12"),sQuery(id+"F0.wireOp",EDGE,"E13"),sQuery(id+"F0.wireOp",EDGE,"E14"),sQuery(id+"F0.wireOp",EDGE,"E15"),sQuery(id+"F0.wireOp",EDGE,"E17.filletArc"),sQuery(id+"F0.wireOp",EDGE,"E18.filletArc"),sQuery(id+"F0.wireOp",EDGE,"E19.filletArc"),sQuery(id+"F0.wireOp",EDGE,"E20.filletArc"),sQuery(id+"F0.wireOp",EDGE,"E25.0"),sQuery(id+"F0.wireOp",EDGE,"E25.1"),sQuery(id+"F0.wireOp",EDGE,"E25.2"),sQuery(id+"F0.wireOp",EDGE,"E25.3"),sQuery(id+"F0.wireOp",EDGE,"E25.4"),sQuery(id+"F0.wireOp",EDGE,"E25.5"),sQuery(id+"F0.wireOp",EDGE,"E25.6"),sQuery(id+"F0.wireOp",EDGE,"E25.7")])],"isStart":false});
            var Q1;
            Q1 = qSketchRegion(id + "F17", true);
            extrude(context, id + "F18", {"entities" : qUnion([Q0, Q1]), "depth" : 25 * mm});
        }
    });
